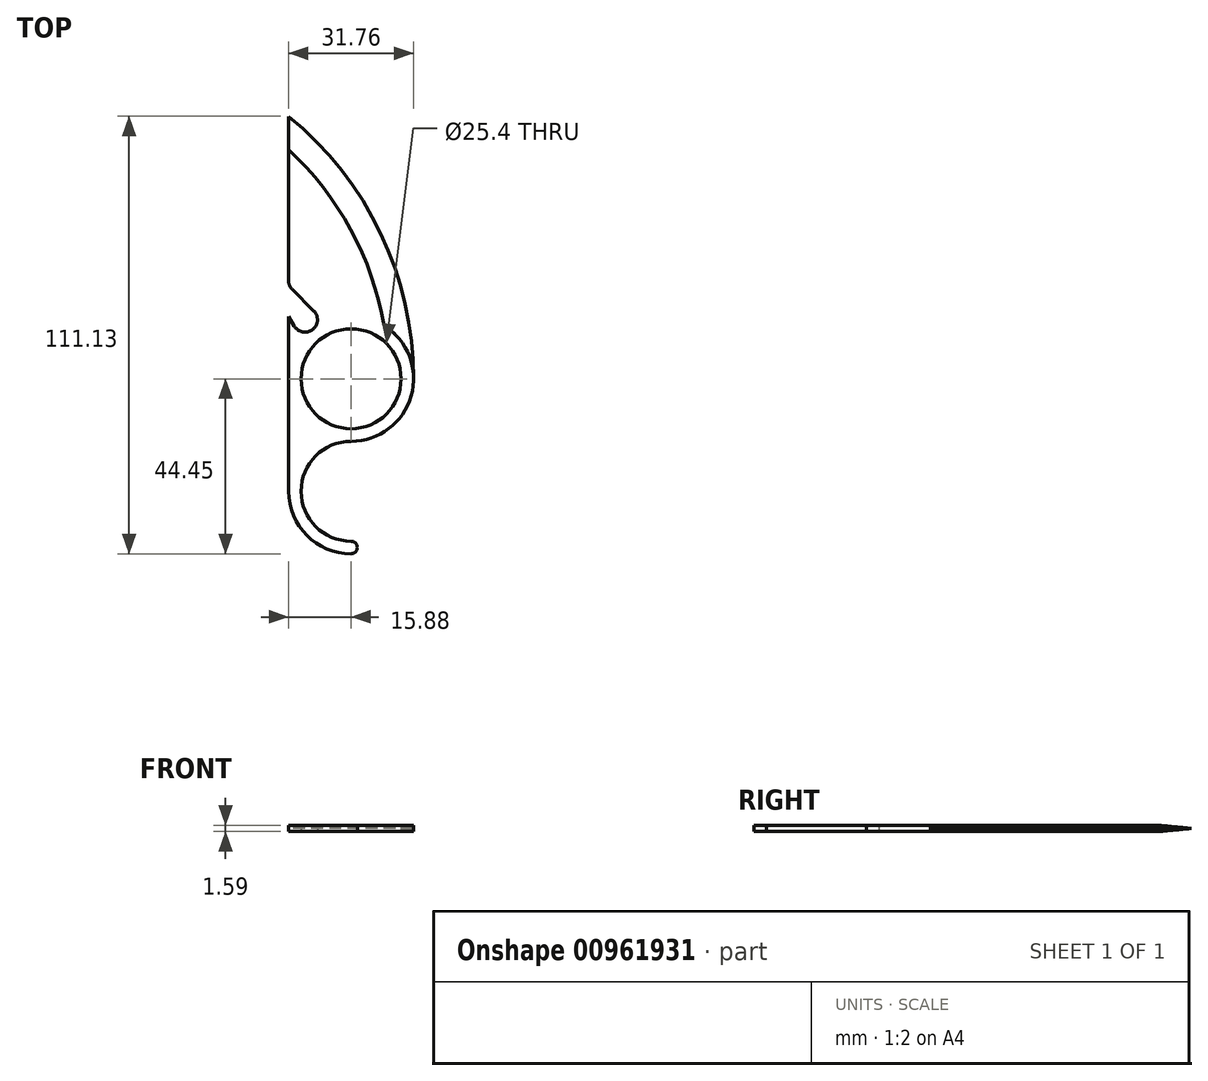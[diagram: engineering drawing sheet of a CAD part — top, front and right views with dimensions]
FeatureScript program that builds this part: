
annotation { "Feature Type Name" : "Feature", "Feature Type Description" : "" }
export const myFeature = defineFeature(function(context is Context, id is Id, definition is map)
    precondition{}
    {
        {
            var Q0;
            Q0=qCreatedBy(makeId("Top.planeOp"),FACE);
            var sketch = newSketch(context, id + "F0", { "sketchPlane" : qUnion([Q0])});
            skCircle(sketch, "E0", {"center": v(0, 0) * mm, "radius": 12.7 * mm});
            skArc(sketch, "E1", {"start": v(15.88, 0) * mm, "mid": v(0, 15.88) * mm, "end": v(-15.88, 0) * mm});
            skArc(sketch, "E2", {"start": v(0, -15.88) * mm, "mid": v(-12.7, -28.58) * mm, "end": v(0, -41.28) * mm});
            skLineSegment(sketch, "E3", {"start": v(-15.88, -28.58) * mm, "end": v(-15.88, 0) * mm});
            skLineSegment(sketch, "E4", {"start": v(-15.88, 0) * mm, "end": v(-15.88, 15.88) * mm});
            skArc(sketch, "E5", {"start": v(15.88, 0) * mm, "mid": v(7.53, 36.92) * mm, "end": v(-15.88, 66.68) * mm});
            skPoint(sketch, "E6", {"position": v(0, 15.88) * mm});
            skLineSegment(sketch, "E7", {"start": v(-15.88, 0) * mm, "end": v(-15.87, 0) * mm});
            skArc(sketch, "E8", {"start": v(0, -15.88) * mm, "mid": v(11.23, -11.23) * mm, "end": v(15.88, 0) * mm});
            skArc(sketch, "E9", {"start": v(-14.47, 13.43) * mm, "mid": v(-9.78, 12.5) * mm, "end": v(-9.47, 17.27) * mm});
            skLineSegment(sketch, "E10", {"start": v(-9.47, 17.27) * mm, "end": v(-14.95, 22.74) * mm});
            skLineSegment(sketch, "E11", {"start": v(-14.47, 13.43) * mm, "end": v(-15.88, 15.88) * mm});
            skLineSegment(sketch, "E12.trimOffspring", {"start": v(-15.88, 24.99) * mm, "end": v(-15.88, 66.68) * mm});
            skPoint(sketch, "E13.visualSharp", {"position": v(-15.88, 23.67) * mm});
            skArc(sketch, "E13.filletArc", {"start": v(-15.88, 24.99) * mm, "mid": v(-15.63, 23.77) * mm, "end": v(-14.95, 22.74) * mm});
            skArc(sketch, "E14", {"start": v(-15.88, -28.58) * mm, "mid": v(-11.23, -39.8) * mm, "end": v(0, -44.45) * mm});
            skArc(sketch, "E15", {"start": v(0, -41.28) * mm, "mid": v(1.59, -42.86) * mm, "end": v(0, -44.45) * mm});
            skSolve(sketch);
        }
        {
            var Q0;
            {var subQ1=sQuery(id+"F0.wireOp",EDGE,"E5");Q0=makeQuery(id+"F0.imprint","IMPRINT",FACE,{"disambiguationData":[TD([[makeQuery(id+"F0.imprint","IMPRINT",EDGE,{"derivedFrom":subQ1}),1.0]])]});}
            extrude(context, id + "F1", {"entities" : qUnion([Q0]), "depth" : 1.59 * mm, "offsetDistance" : 25.4 * mm});
        }
        {
            var Q0;
            Q0=makeQuery(id+"F1.opExtrude","CAP_EDGE",EDGE,{"disambiguationData":[OSD([sQuery(id+"F0.wireOp",EDGE,"E5")])],"isStart":false});
            chamfer(context, id + "F2", {"entities" : qUnion([Q0]), "chamferType" : ChamferType.TWO_OFFSETS, "width1" : 0.8 * mm, "oppositeDirection" : true, "width2" : 6.35 * mm, "tangentPropagation" : true});
        }
        {
            var Q0;
            Q0=makeQuery(id+"F1.opExtrude","CAP_EDGE",EDGE,{"disambiguationData":[OSD([sQuery(id+"F0.wireOp",EDGE,"E5")])],"isStart":true});
            chamfer(context, id + "F3", {"entities" : qUnion([Q0]), "chamferType" : ChamferType.TWO_OFFSETS, "width1" : 0.8 * mm, "oppositeDirection" : false, "width2" : 6.35 * mm, "tangentPropagation" : true});
        }
        {
            var Q0;
            Q0=makeQuery(id+"F0.imprint","IMPRINT",FACE,{"disambiguationData":[TD([[makeQuery(id+"F0.imprint","IMPRINT",EDGE,{"derivedFrom":sQuery(id+"F0.wireOp",EDGE,"E0")}),-1.0]])]});
            var Q1;
            {var subQ0=sQuery(id+"F0.wireOp",EDGE,"E4");Q1=makeQuery(id+"F0.imprint","IMPRINT",FACE,{"disambiguationData":[TD([[makeQuery(id+"F0.imprint","IMPRINT",EDGE,{"derivedFrom":subQ0}),-1.0]])]});}
            extrude(context, id + "F4", {"entities" : qUnion([Q0, Q1]), "operationType" : NewBodyOperationType.ADD, "depth" : 1.59 * mm, "offsetDistance" : 25.4 * mm});
        }
    });
